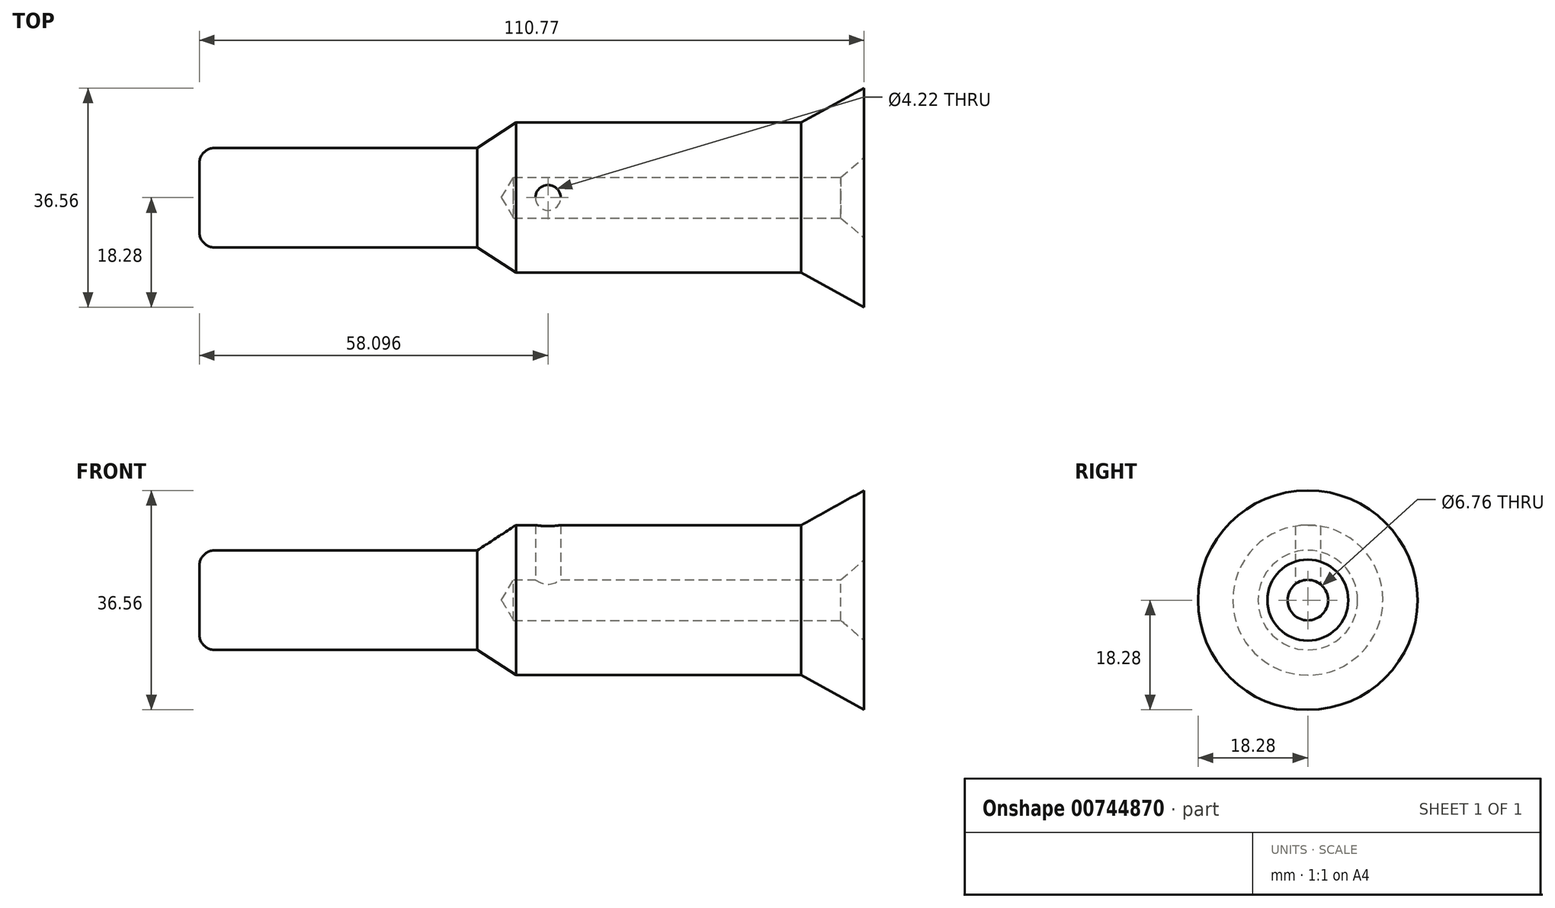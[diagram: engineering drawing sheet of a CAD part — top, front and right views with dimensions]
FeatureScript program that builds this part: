
annotation { "Feature Type Name" : "Feature", "Feature Type Description" : "" }
export const myFeature = defineFeature(function(context is Context, id is Id, definition is map)
    precondition{}
    {
        {
            var Q0;
            Q0=qCreatedBy(makeId("Front.planeOp"),FACE);
            var sketch = newSketch(context, id + "F0", { "sketchPlane" : qUnion([Q0])});
            skLineSegment(sketch, "E0", {"start": v(-170.75, 0) * mm, "end": v(147.23, 0) * mm, "construction": true});
            skLineSegment(sketch, "E1", {"start": v(-52.77, 0) * mm, "end": v(-52.77, 8.3) * mm});
            skLineSegment(sketch, "E2", {"start": v(-52.77, 8.3) * mm, "end": v(-6.46, 8.3) * mm});
            skLineSegment(sketch, "E3", {"start": v(-6.46, 8.3) * mm, "end": v(0, 12.5) * mm});
            skLineSegment(sketch, "E4", {"start": v(0, 12.5) * mm, "end": v(47.52, 12.5) * mm});
            skLineSegment(sketch, "E5", {"start": v(58, 12.5) * mm, "end": v(58, 0) * mm});
            skLineSegment(sketch, "E6", {"start": v(-52.77, 0) * mm, "end": v(58, 0) * mm});
            skLineSegment(sketch, "E7", {"start": v(47.52, 12.5) * mm, "end": v(58, 18.28) * mm});
            skLineSegment(sketch, "E8", {"start": v(58, 18.28) * mm, "end": v(58, 12.5) * mm});
            skSolve(sketch);
        }
        {
            var Q0;
            Q0 = qSketchRegion(id + "F0", true);
            var Q1;
            Q1=sQuery(id+"F0.wireOp",EDGE,"E0");
            revolve(context, id + "F1", {"surfaceOperationType" : NewSurfaceOperationType.NEW, "entities" : qUnion([Q0]), "axis" : qUnion([Q1]), "revolveType" : RevolveType.FULL});
        }
        {
            var Q0;
            Q0=makeQuery(id+"F1.opRevolve","SWEPT_EDGE",EDGE,{"disambiguationData":[OSD([sQuery(id+"F0.wireOp",EDGE,"E1"),sQuery(id+"F0.wireOp",EDGE,"E2")])]});
            fillet(context, id + "F2", {"entities" : qUnion([Q0]), "radius" : 2.54 * mm, "tangentPropagation" : true, "allowEdgeOverflow" : false});
        }
        {
            var Q0;
            Q0=makeQuery(id+"F1.opRevolve","SWEPT_FACE",FACE,{"disambiguationData":[OSD([sQuery(id+"F0.wireOp",EDGE,"E5")])]});
            var sketch = newSketch(context, id + "F3", { "sketchPlane" : qUnion([Q0])});
            skPoint(sketch, "E9", {"position": v(0, 0) * mm});
            skSolve(sketch);
        }
        {
            var Q0;
            Q0=sQuery(id+"F3.wireOp",VERTEX,"E9");
            var Q1;
            Q1=makeQuery(id+"F1.opRevolve","SWEPT_BODY",BODY,{"disambiguationData":[OSD([sQuery(id+"F0.wireOp",EDGE,"E1"),sQuery(id+"F0.wireOp",EDGE,"E2"),sQuery(id+"F0.wireOp",EDGE,"E3"),sQuery(id+"F0.wireOp",EDGE,"E4"),sQuery(id+"F0.wireOp",EDGE,"E5"),sQuery(id+"F0.wireOp",EDGE,"E6")])]});
            hole(context, id + "F4", {"style" : HoleStyle.C_SINK, "endStyle" : HoleEndStyle.BLIND, "standardTappedOrClearance" : lookupTablePath({ "standard" : "ANSI", "fit" : "Normal (ASME)", "size" : "1/4", "type" : "Clearance" }), "standardBlindInLast" : lookupTablePath({ "fit" : "Free", "standard" : "ANSI", "size" : "1/4", "type" : "Clearance" }), "holeDiameter" : 6.76 * mm, "cSinkDiameter" : 13.5 * mm, "cSinkAngle" : 82 * degree, "majorDiameter" : 6.35 * mm, "holeDepth" : 58.42 * mm, "isTappedThrough" : true, "tappedDepth" : 12.7 * mm, "tapClearance" : 3, "locations" : qUnion([Q0]), "scope" : qUnion([Q1])});
        }
        {
            var Q0;
            Q0=qCreatedBy(makeId("Top.planeOp"),FACE);
            var sketch = newSketch(context, id + "F5", { "sketchPlane" : qUnion([Q0])});
            skPoint(sketch, "E10", {"position": v(5.33, 0) * mm});
            skSolve(sketch);
        }
        {
            var Q0;
            Q0=sQuery(id+"F5.wireOp",VERTEX,"E10");
            var Q1;
            Q1=makeQuery(id+"F1.opRevolve","SWEPT_BODY",BODY,{"disambiguationData":[OSD([sQuery(id+"F0.wireOp",EDGE,"E1"),sQuery(id+"F0.wireOp",EDGE,"E2"),sQuery(id+"F0.wireOp",EDGE,"E3"),sQuery(id+"F0.wireOp",EDGE,"E4"),sQuery(id+"F0.wireOp",EDGE,"E5"),sQuery(id+"F0.wireOp",EDGE,"E6")])]});
            hole(context, id + "F6", {"style" : HoleStyle.SIMPLE, "endStyle" : HoleEndStyle.THROUGH, "oppositeDirection" : true, "holeDiameter" : 4.22 * mm, "majorDiameter" : 6.35 * mm, "isTappedThrough" : true, "tappedDepth" : 12.7 * mm, "tapClearance" : 3, "startFromSketch" : true, "locations" : qUnion([Q0]), "scope" : qUnion([Q1])});
        }
    });
